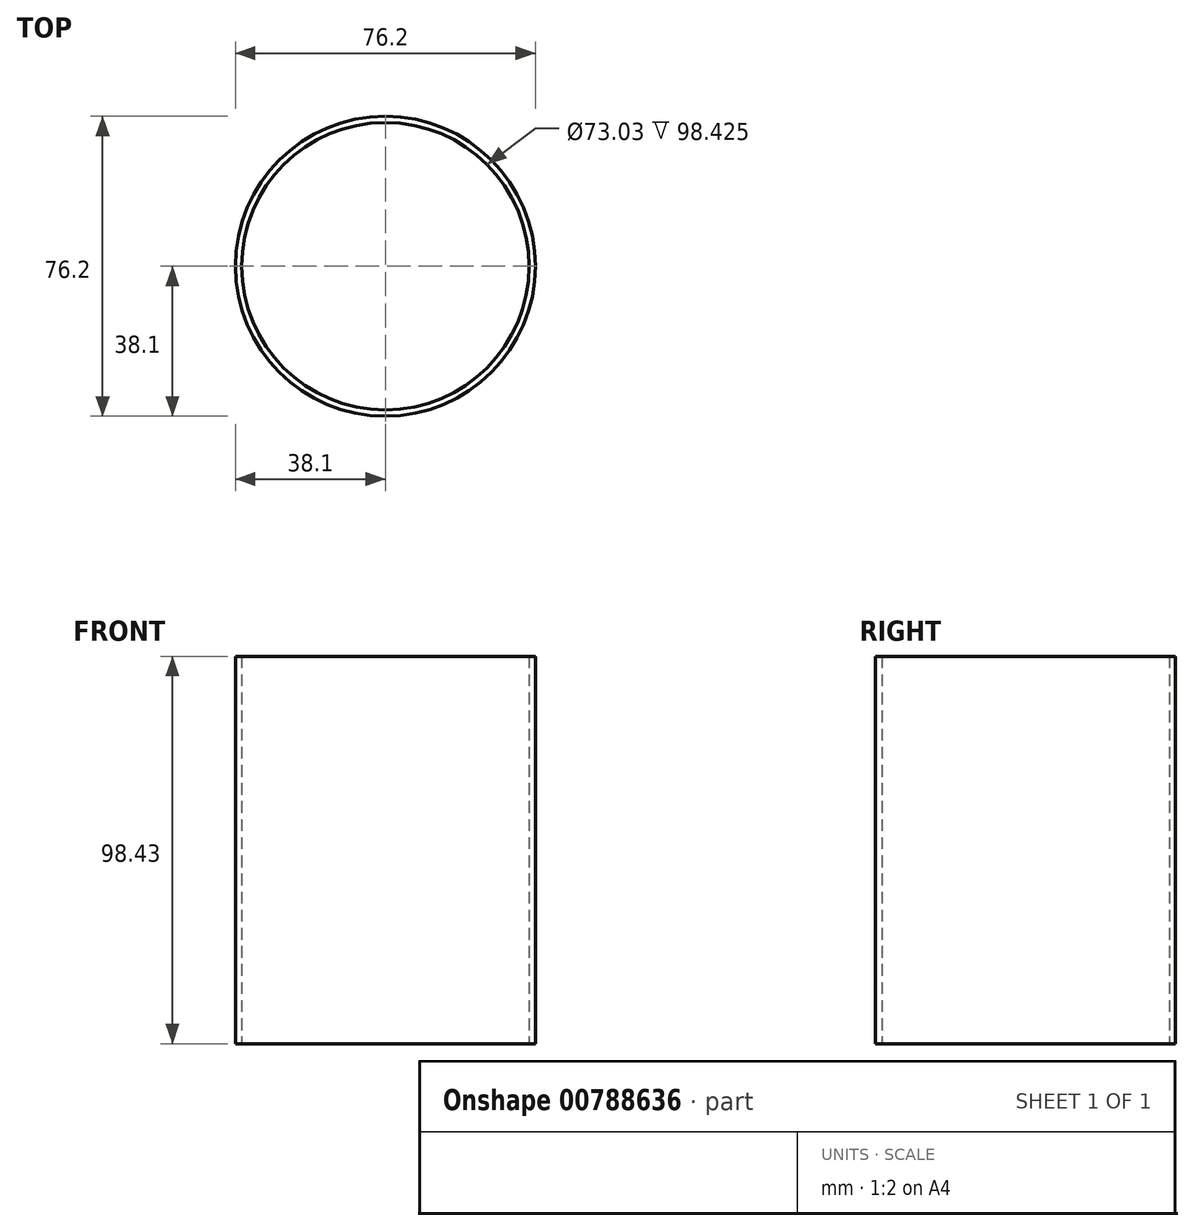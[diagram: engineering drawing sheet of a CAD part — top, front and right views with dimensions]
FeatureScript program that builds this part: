
annotation { "Feature Type Name" : "Feature", "Feature Type Description" : "" }
export const myFeature = defineFeature(function(context is Context, id is Id, definition is map)
    precondition{}
    {
        {
            var Q0;
            Q0=qCreatedBy(makeId("Top.planeOp"),FACE);
            var sketch = newSketch(context, id + "F0", { "sketchPlane" : qUnion([Q0])});
            skCircle(sketch, "E0", {"center": v(0, 0) * mm, "radius": 38.1 * mm});
            skCircle(sketch, "E1", {"center": v(0, 0) * mm, "radius": 36.51 * mm});
            skSolve(sketch);
        }
        {
            var Q0;
            Q0=makeQuery(id+"F0.imprint","IMPRINT",FACE,{"disambiguationData":[TD([[makeQuery(id+"F0.imprint","IMPRINT",EDGE,{"derivedFrom":sQuery(id+"F0.wireOp",EDGE,"E0")}),1.0]])]});
            extrude(context, id + "F1", {"entities" : qUnion([Q0]), "depth" : 98.42 * mm, "offsetDistance" : 25.4 * mm});
        }
    });
